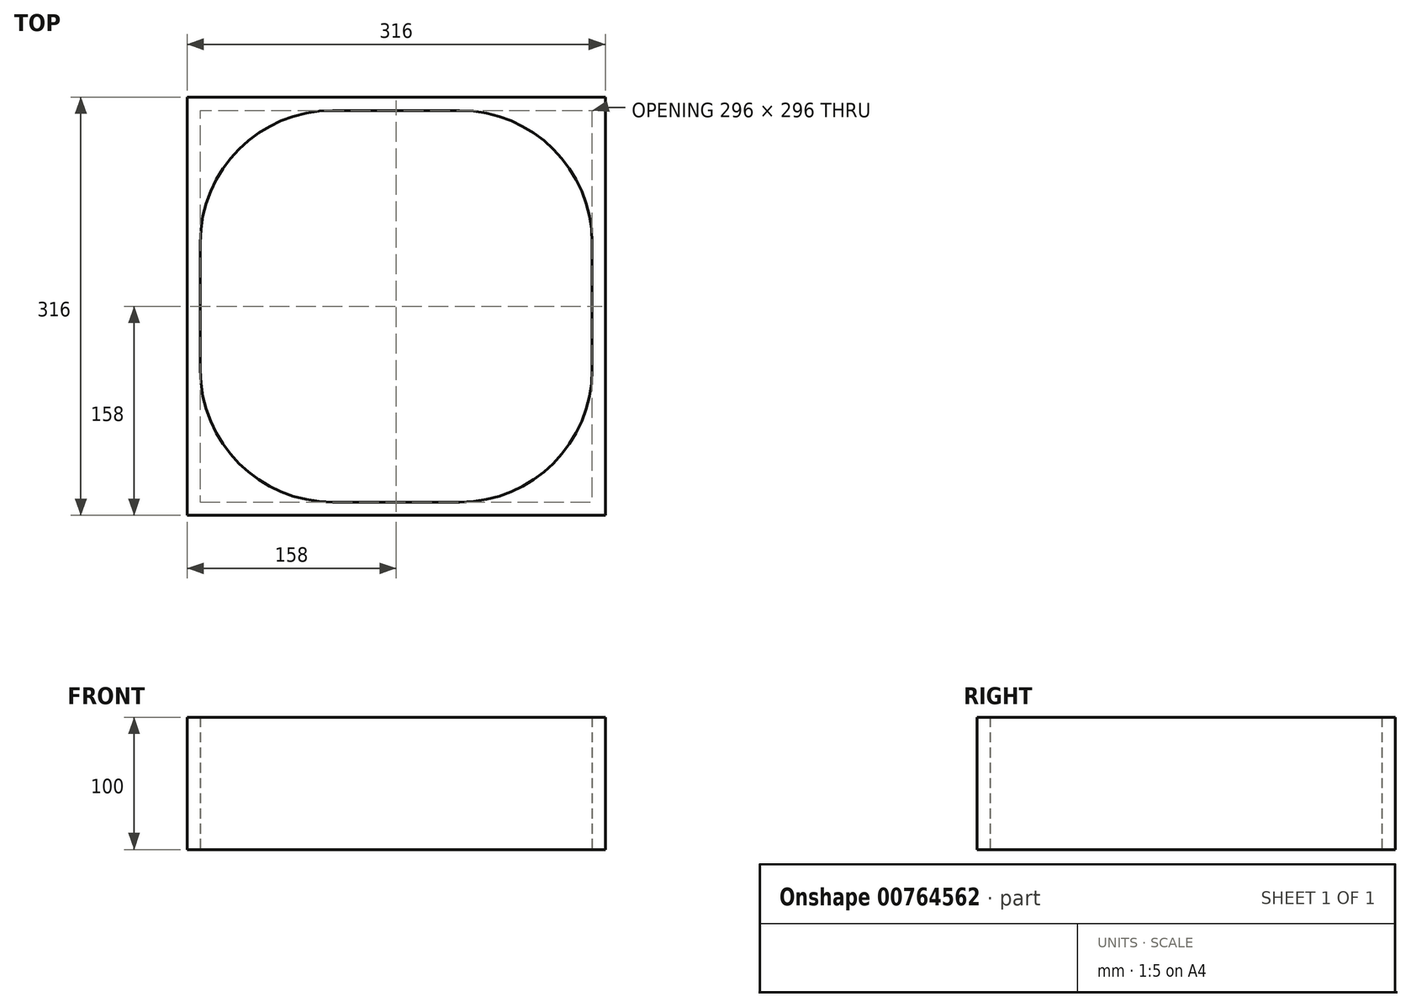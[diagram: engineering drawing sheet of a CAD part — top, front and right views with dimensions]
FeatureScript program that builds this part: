
annotation { "Feature Type Name" : "Feature", "Feature Type Description" : "" }
export const myFeature = defineFeature(function(context is Context, id is Id, definition is map)
    precondition{}
    {
        {
            var Q0;
            Q0=qCreatedBy(makeId("Top.planeOp"),FACE);
            var sketch = newSketch(context, id + "F0", { "sketchPlane" : qUnion([Q0])});
            skLineSegment(sketch, "E0.bottom", {"start": v(-48, 148) * mm, "end": v(48, 148) * mm});
            skLineSegment(sketch, "E0.top", {"start": v(-48, -148) * mm, "end": v(48, -148) * mm});
            skLineSegment(sketch, "E0.left", {"start": v(-148, 48) * mm, "end": v(-148, -48) * mm});
            skLineSegment(sketch, "E0.right", {"start": v(148, 48) * mm, "end": v(148, -48) * mm});
            skPoint(sketch, "E1.visualSharp", {"position": v(148, 148) * mm});
            skArc(sketch, "E1.filletArc", {"start": v(148, 48) * mm, "mid": v(118.71, 118.71) * mm, "end": v(48, 148) * mm});
            skPoint(sketch, "E2.visualSharp", {"position": v(148, -148) * mm});
            skArc(sketch, "E2.filletArc", {"start": v(48, -148) * mm, "mid": v(118.71, -118.71) * mm, "end": v(148, -48) * mm});
            skPoint(sketch, "E3.visualSharp", {"position": v(-148, 148) * mm});
            skArc(sketch, "E3.filletArc", {"start": v(-48, 148) * mm, "mid": v(-118.71, 118.71) * mm, "end": v(-148, 48) * mm});
            skPoint(sketch, "E4.visualSharp", {"position": v(-148, -148) * mm});
            skArc(sketch, "E4.filletArc", {"start": v(-148, -48) * mm, "mid": v(-118.71, -118.71) * mm, "end": v(-48, -148) * mm});
            skLineSegment(sketch, "E5.bottom", {"start": v(-158, 158) * mm, "end": v(158, 158) * mm});
            skLineSegment(sketch, "E5.top", {"start": v(-158, -158) * mm, "end": v(158, -158) * mm});
            skLineSegment(sketch, "E5.left", {"start": v(-158, 158) * mm, "end": v(-158, -158) * mm});
            skLineSegment(sketch, "E5.right", {"start": v(158, 158) * mm, "end": v(158, -158) * mm});
            skSolve(sketch);
        }
        {
            var Q0;
            Q0 = qSketchRegion(id + "F0", true);
            extrude(context, id + "F1", {"entities" : qUnion([Q0]), "endBound" : BoundingType.SYMMETRIC, "depth" : 100 * mm, "offsetDistance" : 25 * mm});
        }
    });
